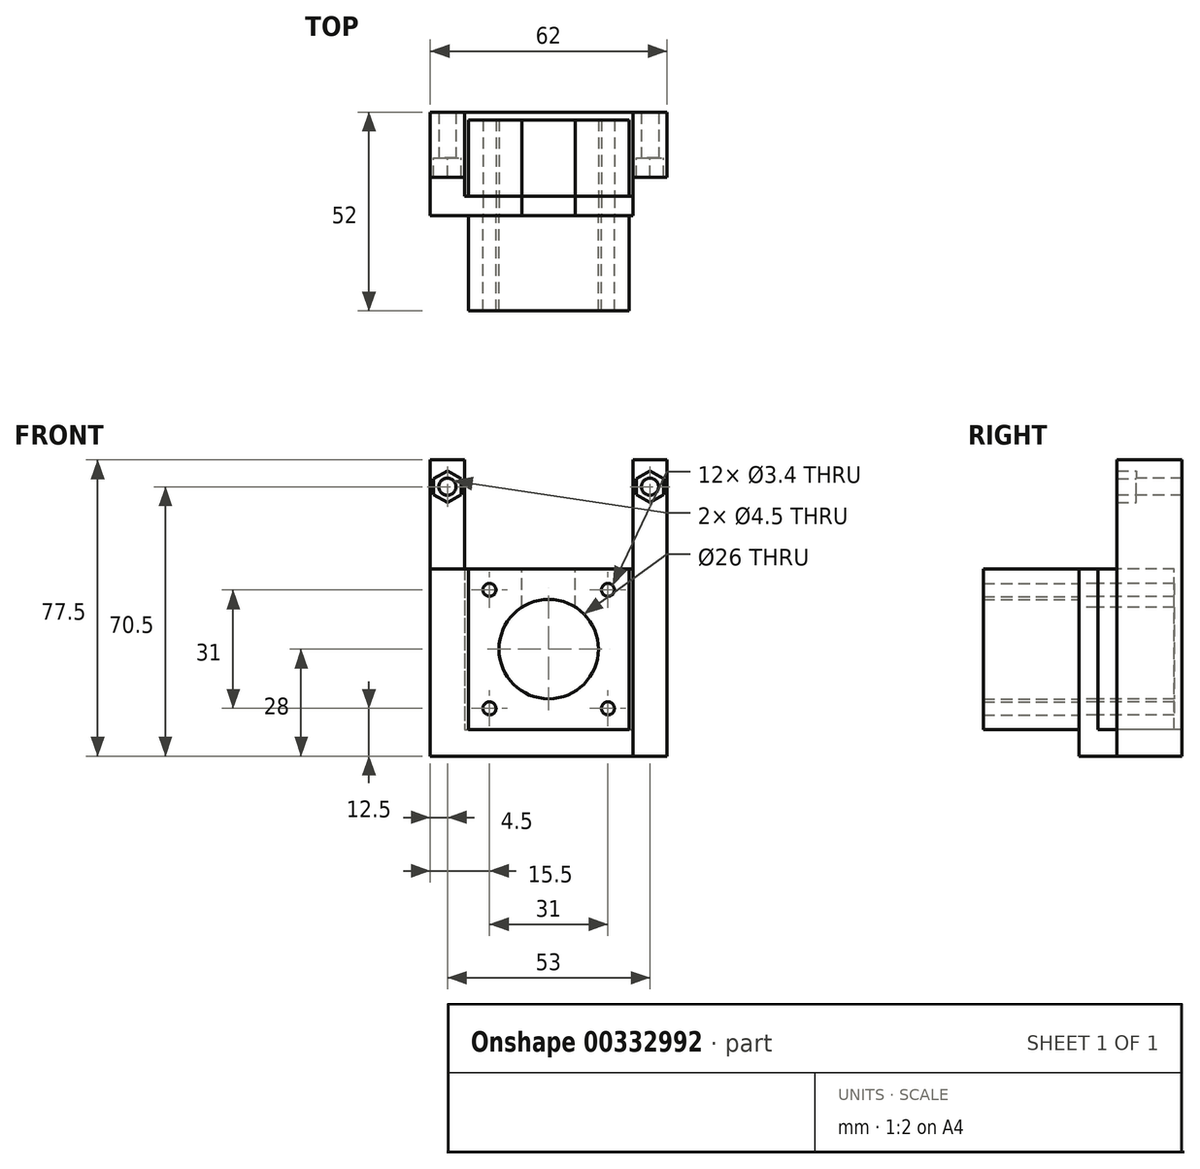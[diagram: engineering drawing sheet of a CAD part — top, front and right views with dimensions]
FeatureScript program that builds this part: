
annotation { "Feature Type Name" : "Feature", "Feature Type Description" : "" }
export const myFeature = defineFeature(function(context is Context, id is Id, definition is map)
    precondition{}
    {
        {
            assignVariable(context, id + "F0", {"name" : "MotorLength", "anyValue" : 20});
        }
        {
            var Q0;
            Q0=qCreatedBy(makeId("Front.planeOp"),FACE);
            var sketch = newSketch(context, id + "F1", { "sketchPlane" : qUnion([Q0])});
            skCircle(sketch, "E0", {"center": v(0, 0) * mm, "radius": 2.25 * mm});
            skCircle(sketch, "E1", {"center": v(-31.5, 49.5) * mm, "radius": 2.25 * mm});
            skCircle(sketch, "E2", {"center": v(21.5, 49.5) * mm, "radius": 2.25 * mm});
            skPoint(sketch, "E3", {"position": v(-36, 56.5) * mm});
            skPoint(sketch, "E4", {"position": v(-27, 56.5) * mm});
            skPoint(sketch, "E5", {"position": v(-27, -14) * mm});
            skLineSegment(sketch, "E6", {"start": v(-36, 56.5) * mm, "end": v(-27, 56.5) * mm});
            skLineSegment(sketch, "E7", {"start": v(-27, 56.5) * mm, "end": v(-27, -14) * mm});
            skLineSegment(sketch, "E8", {"start": v(-27, -14) * mm, "end": v(17, -14) * mm});
            skLineSegment(sketch, "E9", {"start": v(17, -14) * mm, "end": v(17, 56.5) * mm});
            skLineSegment(sketch, "E10", {"start": v(17, 56.5) * mm, "end": v(26, 56.5) * mm});
            skPoint(sketch, "E11", {"position": v(-36, -21) * mm});
            skLineSegment(sketch, "E12", {"start": v(-36, 56.5) * mm, "end": v(-36, -21) * mm});
            skLineSegment(sketch, "E13", {"start": v(-36, -21) * mm, "end": v(26, -21) * mm});
            skLineSegment(sketch, "E14", {"start": v(26, 56.5) * mm, "end": v(26, -21) * mm});
            skSolve(sketch);
        }
        {
            var Q0;
            Q0=makeQuery(id+"F1.imprint","IMPRINT",FACE,{"disambiguationData":[TD([[makeQuery(id+"F1.imprint","IMPRINT",EDGE,{"derivedFrom":sQuery(id+"F1.wireOp",EDGE,"E1")}),-1.0]])]});
            extrude(context, id + "F2", {"entities" : qUnion([Q0]), "oppositeDirection" : true, "depth" : 12 * mm});
        }
        {
            var Q0;
            Q0=makeQuery(id+"F2.opExtrude","CAP_FACE",FACE,{"disambiguationData":[OSD([sQuery(id+"F1.wireOp",EDGE,"E1"),sQuery(id+"F1.wireOp",EDGE,"E2"),sQuery(id+"F1.wireOp",EDGE,"E6"),sQuery(id+"F1.wireOp",EDGE,"E7"),sQuery(id+"F1.wireOp",EDGE,"E8"),sQuery(id+"F1.wireOp",EDGE,"E9"),sQuery(id+"F1.wireOp",EDGE,"E10"),sQuery(id+"F1.wireOp",EDGE,"E12"),sQuery(id+"F1.wireOp",EDGE,"E13"),sQuery(id+"F1.wireOp",EDGE,"E14")])],"isStart":true});
            var sketch = newSketch(context, id + "F3", { "sketchPlane" : qUnion([Q0])});
            skCircle(sketch, "E15.cCircle", {"center": v(-31.5, 49.5) * mm, "radius": 3.6 * mm, "construction": true});
            skLineSegment(sketch, "E15.0", {"start": v(-27.9, 51.58) * mm, "end": v(-27.9, 47.42) * mm});
            skLineSegment(sketch, "E15.1", {"start": v(-27.9, 47.42) * mm, "end": v(-31.5, 45.34) * mm});
            skLineSegment(sketch, "E15.2", {"start": v(-31.5, 45.34) * mm, "end": v(-35.1, 47.42) * mm});
            skLineSegment(sketch, "E15.3", {"start": v(-35.1, 47.42) * mm, "end": v(-35.1, 51.58) * mm});
            skLineSegment(sketch, "E15.4", {"start": v(-35.1, 51.58) * mm, "end": v(-31.5, 53.66) * mm});
            skLineSegment(sketch, "E15.5", {"start": v(-31.5, 53.66) * mm, "end": v(-27.9, 51.58) * mm});
            skPoint(sketch, "E15.0.midPoint", {"position": v(-27.9, 49.5) * mm});
            skCircle(sketch, "E16.cCircle", {"center": v(21.5, 49.5) * mm, "radius": 3.6 * mm, "construction": true});
            skLineSegment(sketch, "E16.0", {"start": v(25.1, 51.58) * mm, "end": v(25.1, 47.42) * mm});
            skLineSegment(sketch, "E16.1", {"start": v(25.1, 47.42) * mm, "end": v(21.5, 45.34) * mm});
            skLineSegment(sketch, "E16.2", {"start": v(21.5, 45.34) * mm, "end": v(17.9, 47.42) * mm});
            skLineSegment(sketch, "E16.3", {"start": v(17.9, 47.42) * mm, "end": v(17.9, 51.58) * mm});
            skLineSegment(sketch, "E16.4", {"start": v(17.9, 51.58) * mm, "end": v(21.5, 53.66) * mm});
            skLineSegment(sketch, "E16.5", {"start": v(21.5, 53.66) * mm, "end": v(25.1, 51.58) * mm});
            skPoint(sketch, "E16.0.midPoint", {"position": v(25.1, 49.5) * mm});
            skSolve(sketch);
        }
        {
            var Q0;
            Q0=makeQuery(id+"F3.imprint","IMPRINT",FACE,{"disambiguationData":[TD([[makeQuery(id+"F3.imprint","IMPRINT",EDGE,{"derivedFrom":sQuery(id+"F3.wireOp",EDGE,"E15.0")}),1.0]])]});
            extrude(context, id + "F4", {"entities" : qUnion([Q0]), "operationType" : NewBodyOperationType.ADD, "depth" : 5 * mm});
        }
        {
            var Q0;
            {var subQ0=sQuery(id+"F1.wireOp",EDGE,"E8");Q0=makeQuery(id+"F4.boolean.opBoolean","MERGE",FACE,{"derivedFrom":[makeQuery(id+"F2.opExtrude","SWEPT_FACE",FACE,{"disambiguationData":[OSD([subQ0])]}),makeQuery(id+"F4.opExtrude","SWEPT_FACE",FACE,{"disambiguationData":[OSD([subQ0])]})]});}
            var sketch = newSketch(context, id + "F5", { "sketchPlane" : qUnion([Q0])});
            skLineSegment(sketch, "E17.0", {"start": v(-27, 12) * mm, "end": v(17, 12) * mm});
            skPoint(sketch, "E18.oppositeSnap0", {"position": v(17, 3.5) * mm});
            skLineSegment(sketch, "E18.top", {"start": v(-27, -10) * mm, "end": v(17, -10) * mm});
            skLineSegment(sketch, "E18.left", {"start": v(-27, 12) * mm, "end": v(-27, -10) * mm});
            skLineSegment(sketch, "E18.right", {"start": v(17, 12) * mm, "end": v(17, -10) * mm});
            skLineSegment(sketch, "E19.top", {"start": v(-27, -15) * mm, "end": v(17, -15) * mm});
            skLineSegment(sketch, "E19.left", {"start": v(-27, -10) * mm, "end": v(-27, -15) * mm});
            skLineSegment(sketch, "E19.right", {"start": v(17, -10) * mm, "end": v(17, -15) * mm});
            skLineSegment(sketch, "E20.0", {"start": v(17, -5) * mm, "end": v(26, -5) * mm});
            skLineSegment(sketch, "E21.bottom", {"start": v(26, -5) * mm, "end": v(17, -5) * mm});
            skLineSegment(sketch, "E21.top", {"start": v(26, -15) * mm, "end": v(17, -15) * mm});
            skLineSegment(sketch, "E21.left", {"start": v(26, -5) * mm, "end": v(26, -15) * mm});
            skLineSegment(sketch, "E21.right", {"start": v(17, -5) * mm, "end": v(17, -15) * mm});
            skLineSegment(sketch, "E22.0", {"start": v(-36, -5) * mm, "end": v(-27, -5) * mm});
            skLineSegment(sketch, "E23.top", {"start": v(-36, -15) * mm, "end": v(-27, -15) * mm});
            skLineSegment(sketch, "E23.left", {"start": v(-36, -5) * mm, "end": v(-36, -15) * mm});
            skLineSegment(sketch, "E23.right", {"start": v(-27, -5) * mm, "end": v(-27, -15) * mm});
            skSolve(sketch);
        }
        {
            var Q0;
            {var subQ0=sQuery(id+"F5.wireOp",EDGE,"E18.top");Q0=makeQuery(id+"F5.imprint","IMPRINT",FACE,{"disambiguationData":[TD([[makeQuery(id+"F5.imprint","IMPRINT",EDGE,{"derivedFrom":subQ0}),1.0]])]});}
            var Q1;
            {var subQ0=sQuery(id+"F5.wireOp",EDGE,"E18.top");Q1=makeQuery(id+"F5.imprint","IMPRINT",FACE,{"disambiguationData":[TD([[makeQuery(id+"F5.imprint","IMPRINT",EDGE,{"derivedFrom":subQ0}),-1.0]])]});}
            var Q2;
            {var subQ1=sQuery(id+"F5.wireOp",EDGE,"E22.0");Q2=makeQuery(id+"F5.imprint","IMPRINT",FACE,{"disambiguationData":[TD([[makeQuery(id+"F5.imprint","IMPRINT",EDGE,{"derivedFrom":subQ1}),-1.0]])]});}
            var Q3;
            {var subQ1=sQuery(id+"F5.wireOp",EDGE,"E21.bottom");Q3=makeQuery(id+"F5.imprint","IMPRINT",FACE,{"disambiguationData":[TD([[makeQuery(id+"F5.imprint","IMPRINT",EDGE,{"derivedFrom":subQ1}),1.0]])]});}
            var Q4;
            {var subQ0=sQuery(id+"F1.wireOp",EDGE,"E13");Q4=makeQuery(id+"F4.boolean.opBoolean","MERGE",FACE,{"derivedFrom":[makeQuery(id+"F2.opExtrude","SWEPT_FACE",FACE,{"disambiguationData":[OSD([subQ0])]}),makeQuery(id+"F4.opExtrude","SWEPT_FACE",FACE,{"disambiguationData":[OSD([subQ0])]})]});}
            extrude(context, id + "F6", {"entities" : qUnion([Q0, Q1, Q2, Q3]), "operationType" : NewBodyOperationType.ADD, "endBound" : BoundingType.UP_TO_SURFACE, "oppositeDirection" : true, "endBoundEntityFace" : qUnion([Q4]), "depth" : 25 * mm});
        }
        {
            var Q0;
            {var subQ0=sQuery(id+"F5.wireOp",EDGE,"E18.top");Q0=makeQuery(id+"F5.imprint","IMPRINT",FACE,{"disambiguationData":[TD([[makeQuery(id+"F5.imprint","IMPRINT",EDGE,{"derivedFrom":subQ0}),-1.0]])]});}
            var Q1;
            {var subQ1=sQuery(id+"F5.wireOp",EDGE,"E22.0");Q1=makeQuery(id+"F5.imprint","IMPRINT",FACE,{"disambiguationData":[TD([[makeQuery(id+"F5.imprint","IMPRINT",EDGE,{"derivedFrom":subQ1}),-1.0]])]});}
            var Q2;
            {var subQ1=sQuery(id+"F5.wireOp",EDGE,"E21.bottom");Q2=makeQuery(id+"F5.imprint","IMPRINT",FACE,{"disambiguationData":[TD([[makeQuery(id+"F5.imprint","IMPRINT",EDGE,{"derivedFrom":subQ1}),1.0]])]});}
            extrude(context, id + "F7", {"entities" : qUnion([Q0, Q1, Q2]), "operationType" : NewBodyOperationType.ADD, "depth" : 42 * mm});
        }
        {
            var Q0;
            {var subQ0=sQuery(id+"F5.wireOp",EDGE,"E23.top");var subQ1=sQuery(id+"F5.wireOp",EDGE,"E21.top");var subQ2=sQuery(id+"F5.wireOp",EDGE,"E19.top");Q0=makeQuery(id+"F7.boolean.opBoolean","MERGE",FACE,{"derivedFrom":[makeQuery(id+"F6.opExtrude","SWEPT_FACE",FACE,{"disambiguationData":[OSD([subQ2,subQ1,subQ0])]}),makeQuery(id+"F7.opExtrude","SWEPT_FACE",FACE,{"disambiguationData":[OSD([subQ2,subQ1,subQ0])]})]});}
            var sketch = newSketch(context, id + "F8", { "sketchPlane" : qUnion([Q0])});
            skLineSegment(sketch, "E24.0", {"start": v(-26, -14) * mm, "end": v(16, -14) * mm});
            skPoint(sketch, "E25", {"position": v(-5, -14) * mm});
            skPoint(sketch, "E26", {"position": v(-26, -14) * mm});
            skPoint(sketch, "E27", {"position": v(16, -14) * mm});
            skPoint(sketch, "E28.orphan", {"position": v(-27, -14) * mm});
            skPoint(sketch, "E29.orphan", {"position": v(17, -14) * mm});
            skPoint(sketch, "E30", {"position": v(-26, 28) * mm});
            skPoint(sketch, "E31", {"position": v(16, 28) * mm});
            skLineSegment(sketch, "E32", {"start": v(-26, 28) * mm, "end": v(16, -14) * mm, "construction": true});
            skLineSegment(sketch, "E33", {"start": v(-26, -14) * mm, "end": v(16, 28) * mm, "construction": true});
            skPoint(sketch, "E34", {"position": v(-5, 7) * mm});
            skCircle(sketch, "E35", {"center": v(-5, 7) * mm, "radius": 13 * mm});
            skCircle(sketch, "E36", {"center": v(-20.5, 22.5) * mm, "radius": 1.7 * mm});
            skCircle(sketch, "E37.1.0", {"center": v(-20.5, -8.5) * mm, "radius": 1.7 * mm});
            skCircle(sketch, "E37.2.0", {"center": v(10.5, -8.5) * mm, "radius": 1.7 * mm});
            skCircle(sketch, "E37.3.0", {"center": v(10.5, 22.5) * mm, "radius": 1.7 * mm});
            skSolve(sketch);
        }
        {
            var Q0;
            Q0=makeQuery(id+"F8.imprint","IMPRINT",FACE,{"disambiguationData":[TD([[makeQuery(id+"F8.imprint","IMPRINT",EDGE,{"derivedFrom":sQuery(id+"F8.wireOp",EDGE,"E36")}),1.0]])]});
            var Q1;
            Q1=makeQuery(id+"F8.imprint","IMPRINT",FACE,{"disambiguationData":[TD([[makeQuery(id+"F8.imprint","IMPRINT",EDGE,{"derivedFrom":sQuery(id+"F8.wireOp",EDGE,"E35")}),1.0]])]});
            var Q2;
            Q2=makeQuery(id+"F8.imprint","IMPRINT",FACE,{"disambiguationData":[TD([[makeQuery(id+"F8.imprint","IMPRINT",EDGE,{"derivedFrom":sQuery(id+"F8.wireOp",EDGE,"E37.1.0")}),1.0]])]});
            var Q3;
            Q3=makeQuery(id+"F8.imprint","IMPRINT",FACE,{"disambiguationData":[TD([[makeQuery(id+"F8.imprint","IMPRINT",EDGE,{"derivedFrom":sQuery(id+"F8.wireOp",EDGE,"E37.2.0")}),1.0]])]});
            var Q4;
            Q4=makeQuery(id+"F8.imprint","IMPRINT",FACE,{"disambiguationData":[TD([[makeQuery(id+"F8.imprint","IMPRINT",EDGE,{"derivedFrom":sQuery(id+"F8.wireOp",EDGE,"E37.3.0")}),1.0]])]});
            var Q5;
            Q5=makeQuery(id+"F7.opExtrude","SWEPT_FACE",FACE,{"disambiguationData":[OSD([sQuery(id+"F5.wireOp",EDGE,"E18.top")])]});
            extrude(context, id + "F9", {"entities" : qUnion([Q0, Q1, Q2, Q3, Q4]), "operationType" : NewBodyOperationType.REMOVE, "endBound" : BoundingType.UP_TO_SURFACE, "oppositeDirection" : true, "endBoundEntityFace" : qUnion([Q5]), "depth" : 25 * mm});
        }
        {
            var Q0;
            Q0=makeQuery(id+"F7.opExtrude","CAP_FACE",FACE,{"disambiguationData":[OSD([sQuery(id+"F5.wireOp",EDGE,"E18.top"),sQuery(id+"F5.wireOp",EDGE,"E19.top"),sQuery(id+"F5.wireOp",EDGE,"E21.bottom"),sQuery(id+"F5.wireOp",EDGE,"E21.top"),sQuery(id+"F5.wireOp",EDGE,"E21.left"),sQuery(id+"F5.wireOp",EDGE,"E21.right"),sQuery(id+"F5.wireOp",EDGE,"E22.0"),sQuery(id+"F5.wireOp",EDGE,"E23.top"),sQuery(id+"F5.wireOp",EDGE,"E23.left"),sQuery(id+"F5.wireOp",EDGE,"E23.right")])],"isStart":false});
            var sketch = newSketch(context, id + "F10", { "sketchPlane" : qUnion([Q0])});
            skLineSegment(sketch, "E38", {"start": v(-5, -15) * mm, "end": v(-5, -10) * mm, "construction": true});
            skLineSegment(sketch, "E39", {"start": v(-5, -10) * mm, "end": v(-12, -10) * mm});
            skLineSegment(sketch, "E40", {"start": v(-5, -10) * mm, "end": v(2, -10) * mm});
            skLineSegment(sketch, "E41.bottom", {"start": v(-12, -10) * mm, "end": v(2, -10) * mm});
            skLineSegment(sketch, "E41.top", {"start": v(-12, -15) * mm, "end": v(2, -15) * mm});
            skLineSegment(sketch, "E41.left", {"start": v(-12, -10) * mm, "end": v(-12, -15) * mm});
            skLineSegment(sketch, "E41.right", {"start": v(2, -10) * mm, "end": v(2, -15) * mm});
            skSolve(sketch);
        }
        {
            var Q0;
            Q0=makeQuery(id+"F10.imprint","IMPRINT",FACE,{"disambiguationData":[TD([[makeQuery(id+"F10.imprint","IMPRINT",EDGE,{"derivedFrom":sQuery(id+"F10.wireOp",EDGE,"E41.top")}),1.0]])]});
            var Q1;
            Q1=makeQuery(id+"F9.boolean.opBoolean","COPY",FACE,{"derivedFrom":makeQuery(id+"F9.opExtrude","SWEPT_FACE",FACE,{"disambiguationData":[OSD([sQuery(id+"F8.wireOp",EDGE,"E35")])]})});
            extrude(context, id + "F11", {"entities" : qUnion([Q0]), "operationType" : NewBodyOperationType.REMOVE, "endBound" : BoundingType.UP_TO_SURFACE, "oppositeDirection" : true, "endBoundEntityFace" : qUnion([Q1]), "depth" : 25 * mm});
        }
        {
            var Q0;
            Q0=makeQuery(id+"F7.opExtrude","SWEPT_FACE",FACE,{"disambiguationData":[OSD([sQuery(id+"F5.wireOp",EDGE,"E18.top")])]});
            var sketch = newSketch(context, id + "F12", { "sketchPlane" : qUnion([Q0])});
            skLineSegment(sketch, "E42.0", {"start": v(26, -14) * mm, "end": v(-16, -14) * mm});
            skLineSegment(sketch, "E43", {"start": v(-16, -14) * mm, "end": v(-16, 28) * mm});
            skLineSegment(sketch, "E44", {"start": v(-16, 28) * mm, "end": v(26, 28) * mm});
            skLineSegment(sketch, "E45", {"start": v(26, 28) * mm, "end": v(26, -14) * mm});
            skSolve(sketch);
        }
        {
            var Q0;
            Q0=makeQuery(id+"F12.imprint","IMPRINT",FACE,{"disambiguationData":[TD([[makeQuery(id+"F12.imprint","IMPRINT",EDGE,{"derivedFrom":sQuery(id+"F12.wireOp",EDGE,"E42.0")}),-1.0]])]});
            var Q1;
            Q1=makeQuery(id+"F12.imprint","IMPRINT",FACE,{"disambiguationData":[TD([[makeQuery(id+"F12.imprint","IMPRINT",EDGE,{"derivedFrom":makeQuery(id+"F9.boolean.opBoolean","COPY",EDGE,{"derivedFrom":makeQuery(id+"F9.opExtrude","CAP_EDGE",EDGE,{"disambiguationData":[OSD([sQuery(id+"F8.wireOp",EDGE,"E35")])],"isStart":false})})}),-1.0]])]});
            var Q2;
            Q2=makeQuery(id+"F12.imprint","IMPRINT",FACE,{"disambiguationData":[TD([[makeQuery(id+"F12.imprint","IMPRINT",EDGE,{"derivedFrom":makeQuery(id+"F9.boolean.opBoolean","COPY",EDGE,{"derivedFrom":makeQuery(id+"F9.opExtrude","CAP_EDGE",EDGE,{"disambiguationData":[OSD([sQuery(id+"F8.wireOp",EDGE,"E36")])],"isStart":false})})}),-1.0]])]});
            var Q3;
            Q3=makeQuery(id+"F12.imprint","IMPRINT",FACE,{"disambiguationData":[TD([[makeQuery(id+"F12.imprint","IMPRINT",EDGE,{"derivedFrom":makeQuery(id+"F9.boolean.opBoolean","COPY",EDGE,{"derivedFrom":makeQuery(id+"F9.opExtrude","CAP_EDGE",EDGE,{"disambiguationData":[OSD([sQuery(id+"F8.wireOp",EDGE,"E37.3.0")])],"isStart":false})})}),-1.0]])]});
            var Q4;
            Q4=makeQuery(id+"F12.imprint","IMPRINT",FACE,{"disambiguationData":[TD([[makeQuery(id+"F12.imprint","IMPRINT",EDGE,{"derivedFrom":makeQuery(id+"F9.boolean.opBoolean","COPY",EDGE,{"derivedFrom":makeQuery(id+"F9.opExtrude","CAP_EDGE",EDGE,{"disambiguationData":[OSD([sQuery(id+"F8.wireOp",EDGE,"E37.2.0")])],"isStart":false})})}),-1.0]])]});
            var Q5;
            Q5=makeQuery(id+"F12.imprint","IMPRINT",FACE,{"disambiguationData":[TD([[makeQuery(id+"F12.imprint","IMPRINT",EDGE,{"derivedFrom":makeQuery(id+"F9.boolean.opBoolean","COPY",EDGE,{"derivedFrom":makeQuery(id+"F9.opExtrude","CAP_EDGE",EDGE,{"disambiguationData":[OSD([sQuery(id+"F8.wireOp",EDGE,"E37.1.0")])],"isStart":false})})}),-1.0]])]});
            extrude(context, id + "F13", {"entities" : qUnion([Q0, Q1, Q2, Q3, Q4, Q5]), "depth" : (getVariable(context, 'MotorLength')) * mm});
        }
        {
            var Q0;
            Q0=makeQuery(id+"F8.imprint","IMPRINT",FACE,{"disambiguationData":[TD([[makeQuery(id+"F8.imprint","IMPRINT",EDGE,{"derivedFrom":sQuery(id+"F8.wireOp",EDGE,"E35")}),-1.0]])]});
            var sketch = newSketch(context, id + "F14", { "sketchPlane" : qUnion([Q0])});
            skLineSegment(sketch, "E46.0", {"start": v(-26, 28) * mm, "end": v(16, -14) * mm, "construction": true});
            skLineSegment(sketch, "E47.0", {"start": v(-26, -14) * mm, "end": v(16, 28) * mm, "construction": true});
            skLineSegment(sketch, "E48.bottom", {"start": v(-26, 28) * mm, "end": v(16, 28) * mm});
            skLineSegment(sketch, "E48.top", {"start": v(-26, -14) * mm, "end": v(16, -14) * mm});
            skLineSegment(sketch, "E48.left", {"start": v(-26, 28) * mm, "end": v(-26, -14) * mm});
            skLineSegment(sketch, "E48.right", {"start": v(16, 28) * mm, "end": v(16, -14) * mm});
            skSolve(sketch);
        }
        {
            var Q0;
            Q0=makeQuery(id+"F14.imprint","IMPRINT",FACE,{"disambiguationData":[TD([[makeQuery(id+"F14.imprint","IMPRINT",EDGE,{"derivedFrom":sQuery(id+"F14.wireOp",EDGE,"E48.bottom")}),-1.0]])]});
            var Q1;
            Q1=makeQuery(id+"F8.imprint","IMPRINT",FACE,{"disambiguationData":[TD([[makeQuery(id+"F8.imprint","IMPRINT",EDGE,{"derivedFrom":sQuery(id+"F8.wireOp",EDGE,"E36")}),1.0]])]});
            var Q2;
            Q2=makeQuery(id+"F8.imprint","IMPRINT",FACE,{"disambiguationData":[TD([[makeQuery(id+"F8.imprint","IMPRINT",EDGE,{"derivedFrom":sQuery(id+"F8.wireOp",EDGE,"E35")}),1.0]])]});
            var Q3;
            Q3=makeQuery(id+"F8.imprint","IMPRINT",FACE,{"disambiguationData":[TD([[makeQuery(id+"F8.imprint","IMPRINT",EDGE,{"derivedFrom":sQuery(id+"F8.wireOp",EDGE,"E37.1.0")}),1.0]])]});
            var Q4;
            Q4=makeQuery(id+"F8.imprint","IMPRINT",FACE,{"disambiguationData":[TD([[makeQuery(id+"F8.imprint","IMPRINT",EDGE,{"derivedFrom":sQuery(id+"F8.wireOp",EDGE,"E37.3.0")}),1.0]])]});
            var Q5;
            Q5=makeQuery(id+"F8.imprint","IMPRINT",FACE,{"disambiguationData":[TD([[makeQuery(id+"F8.imprint","IMPRINT",EDGE,{"derivedFrom":sQuery(id+"F8.wireOp",EDGE,"E37.2.0")}),1.0]])]});
            extrude(context, id + "F15", {"entities" : qUnion([Q0, Q1, Q2, Q3, Q4, Q5]), "depth" : 25 * mm});
        }
    });
